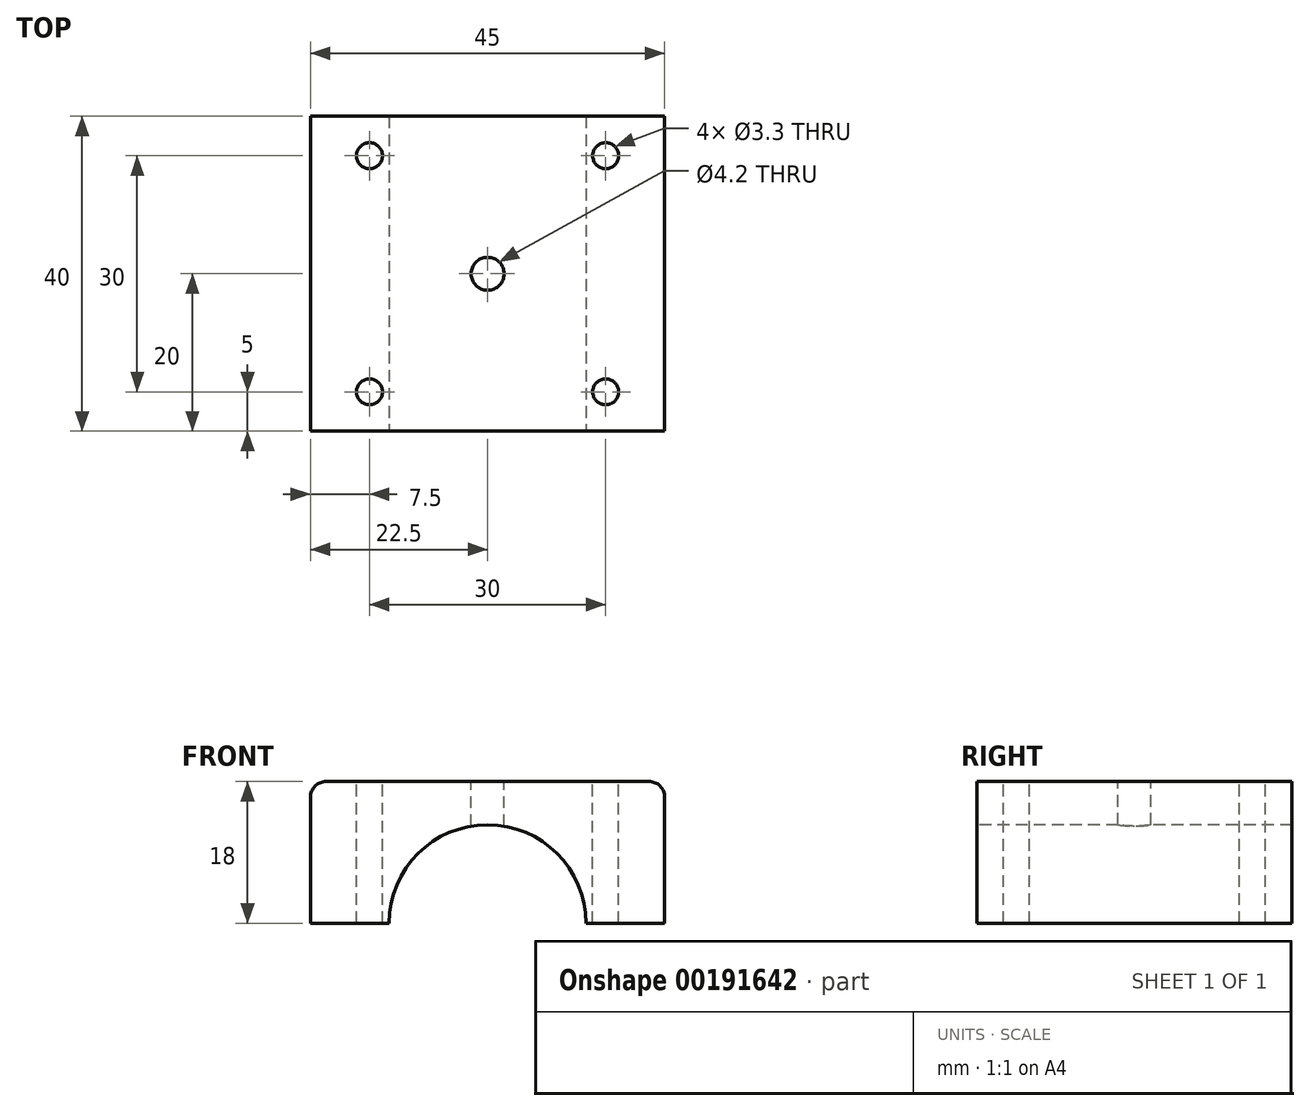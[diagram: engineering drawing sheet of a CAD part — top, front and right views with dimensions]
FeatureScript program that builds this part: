
annotation { "Feature Type Name" : "Feature", "Feature Type Description" : "" }
export const myFeature = defineFeature(function(context is Context, id is Id, definition is map)
    precondition{}
    {
        {
            var Q0;
            Q0=qCreatedBy(makeId("Front.planeOp"),FACE);
            var sketch = newSketch(context, id + "F0", { "sketchPlane" : qUnion([Q0])});
            skLineSegment(sketch, "E0.bottom", {"start": v(25, -6.17) * mm, "end": v(15, -6.17) * mm});
            skLineSegment(sketch, "E0.top", {"start": v(25, 11.83) * mm, "end": v(-20, 11.83) * mm});
            skLineSegment(sketch, "E0.left", {"start": v(25, -6.17) * mm, "end": v(25, 11.83) * mm});
            skLineSegment(sketch, "E0.right", {"start": v(-20, -6.17) * mm, "end": v(-20, 11.83) * mm});
            skArc(sketch, "E1", {"start": v(15, -6.17) * mm, "mid": v(2.5, 6.33) * mm, "end": v(-10, -6.17) * mm});
            skLineSegment(sketch, "E2.trimOffspring", {"start": v(-10, -6.17) * mm, "end": v(-20, -6.17) * mm});
            skSolve(sketch);
        }
        {
            var Q0;
            Q0 = qSketchRegion(id + "F0", true);
            extrude(context, id + "F1", {"entities" : qUnion([Q0]), "oppositeDirection" : true, "depth" : 40 * mm});
        }
        {
            var Q0;
            Q0=makeQuery(id+"F1.opExtrude","SWEPT_FACE",FACE,{"disambiguationData":[OSD([sQuery(id+"F0.wireOp",EDGE,"E0.top")])]});
            var sketch = newSketch(context, id + "F2", { "sketchPlane" : qUnion([Q0])});
            skPoint(sketch, "E3", {"position": v(-12.5, 35) * mm});
            skLineSegment(sketch, "E4", {"start": v(2.5, 40) * mm, "end": v(2.5, 0) * mm, "construction": true});
            skLineSegment(sketch, "E5", {"start": v(-20, 20) * mm, "end": v(25, 20) * mm, "construction": true});
            skPoint(sketch, "E6.MirrorP", {"position": v(17.5, 35) * mm});
            skPoint(sketch, "E7.MirrorP", {"position": v(17.5, 5) * mm});
            skPoint(sketch, "E8.MirrorP", {"position": v(-12.5, 5) * mm});
            skSolve(sketch);
        }
        {
            var Q0;
            Q0=sQuery(id+"F2.wireOp",VERTEX,"E8.MirrorP");
            var Q1;
            Q1=sQuery(id+"F2.wireOp",VERTEX,"E3");
            var Q2;
            Q2=sQuery(id+"F2.wireOp",VERTEX,"E6.MirrorP");
            var Q3;
            Q3=sQuery(id+"F2.wireOp",VERTEX,"E7.MirrorP");
            var Q4;
            Q4=makeQuery(id+"F1.opExtrude","SWEPT_BODY",BODY,{"disambiguationData":[OSD([sQuery(id+"F0.wireOp",EDGE,"E0.bottom"),sQuery(id+"F0.wireOp",EDGE,"E0.top"),sQuery(id+"F0.wireOp",EDGE,"E0.left"),sQuery(id+"F0.wireOp",EDGE,"E0.right"),sQuery(id+"F0.wireOp",EDGE,"E1"),sQuery(id+"F0.wireOp",EDGE,"E2.trimOffspring")])]});
            hole(context, id + "F3", {"style" : HoleStyle.SIMPLE, "endStyle" : HoleEndStyle.THROUGH, "standardTappedOrClearance" : lookupTablePath({ "standard" : "ISO", "fit" : "Normal", "size" : "M3", "type" : "Clearance" }), "standardBlindInLast" : lookupTablePath({ "fit" : "Standard", "standard" : "ISO", "size" : "M3", "type" : "Clearance" }), "holeDiameter" : 3.3 * mm, "locations" : qUnion([Q0, Q1, Q2, Q3]), "scope" : qUnion([Q4]), "isTappedThrough" : true});
        }
        {
            var Q0;
            Q0=makeQuery(id+"F1.opExtrude","SWEPT_FACE",FACE,{"disambiguationData":[OSD([sQuery(id+"F0.wireOp",EDGE,"E0.top")])]});
            var sketch = newSketch(context, id + "F4", { "sketchPlane" : qUnion([Q0])});
            skPoint(sketch, "E9", {"position": v(2.5, 20) * mm});
            skSolve(sketch);
        }
        {
            var Q0;
            Q0=sQuery(id+"F4.wireOp",VERTEX,"E9");
            var Q1;
            Q1=makeQuery(id+"F1.opExtrude","SWEPT_BODY",BODY,{"disambiguationData":[OSD([sQuery(id+"F0.wireOp",EDGE,"E0.bottom"),sQuery(id+"F0.wireOp",EDGE,"E0.top"),sQuery(id+"F0.wireOp",EDGE,"E0.left"),sQuery(id+"F0.wireOp",EDGE,"E0.right"),sQuery(id+"F0.wireOp",EDGE,"E1"),sQuery(id+"F0.wireOp",EDGE,"E2.trimOffspring")])]});
            hole(context, id + "F5", {"style" : HoleStyle.SIMPLE, "endStyle" : HoleEndStyle.THROUGH, "standardTappedOrClearance" : lookupTablePath({ "standard" : "ISO", "fit" : "Close", "size" : "M4", "type" : "Clearance" }), "standardBlindInLast" : lookupTablePath({ "fit" : "Close", "standard" : "ISO", "size" : "M4", "type" : "Clearance" }), "holeDiameter" : 4.2 * mm, "locations" : qUnion([Q0]), "scope" : qUnion([Q1]), "isTappedThrough" : true});
        }
        {
            var Q0;
            Q0=makeQuery(id+"F1.opExtrude","SWEPT_EDGE",EDGE,{"disambiguationData":[OSD([sQuery(id+"F0.wireOp",EDGE,"E0.top"),sQuery(id+"F0.wireOp",EDGE,"E0.right")])]});
            var Q1;
            Q1=makeQuery(id+"F1.opExtrude","SWEPT_EDGE",EDGE,{"disambiguationData":[OSD([sQuery(id+"F0.wireOp",EDGE,"E0.top"),sQuery(id+"F0.wireOp",EDGE,"E0.left")])]});
            fillet(context, id + "F6", {"entities" : qUnion([Q0, Q1]), "radius" : 2 * mm, "tangentPropagation" : true, "allowEdgeOverflow" : false});
        }
        {
            var Q0;
            Q0=qCreatedBy(makeId("Top.planeOp"),FACE);
            var sketch = newSketch(context, id + "F7", { "sketchPlane" : qUnion([Q0])});
            skLineSegment(sketch, "E10", {"start": v(0, 120.41) * mm, "end": v(0, -121.02) * mm, "construction": true});
            skSolve(sketch);
        }
        {
            var Q0;
            Q0=qCreatedBy(makeId("Top.planeOp"),FACE);
            var sketch = newSketch(context, id + "F8", { "sketchPlane" : qUnion([Q0])});
            skLineSegment(sketch, "E11", {"start": v(30, 217.64) * mm, "end": v(-30, 217.64) * mm});
            skLineSegment(sketch, "E12", {"start": v(-30, 217.64) * mm, "end": v(-57.5, 170) * mm});
            skLineSegment(sketch, "E13", {"start": v(-57.5, 170) * mm, "end": v(-57.5, 30) * mm});
            skLineSegment(sketch, "E14", {"start": v(-57.5, 30) * mm, "end": v(-40, -0.3) * mm});
            skLineSegment(sketch, "E15", {"start": v(-40, -0.3) * mm, "end": v(40, -0.3) * mm});
            skLineSegment(sketch, "E16", {"start": v(40, -0.3) * mm, "end": v(57.5, 30) * mm});
            skLineSegment(sketch, "E17", {"start": v(57.5, 30) * mm, "end": v(57.5, 170) * mm});
            skLineSegment(sketch, "E18", {"start": v(57.5, 170) * mm, "end": v(30, 217.64) * mm});
            skSolve(sketch);
        }
        {
            var Q0;
            Q0 = qSketchRegion(id + "F8", true);
            extrude(context, id + "F9", {"entities" : qUnion([Q0]), "depth" : 3 * mm});
        }
        {
            var Q0;
            Q0=makeQuery(id+"F9.opExtrude","SWEPT_BODY",BODY,{"disambiguationData":[OSD([sQuery(id+"F8.wireOp",EDGE,"E11"),sQuery(id+"F8.wireOp",EDGE,"E12"),sQuery(id+"F8.wireOp",EDGE,"E13"),sQuery(id+"F8.wireOp",EDGE,"E14"),sQuery(id+"F8.wireOp",EDGE,"E15"),sQuery(id+"F8.wireOp",EDGE,"E16"),sQuery(id+"F8.wireOp",EDGE,"E17"),sQuery(id+"F8.wireOp",EDGE,"E18")])]});
            deleteBodies(context, id + "F10", {"entities" : qUnion([Q0])});
        }
    });
